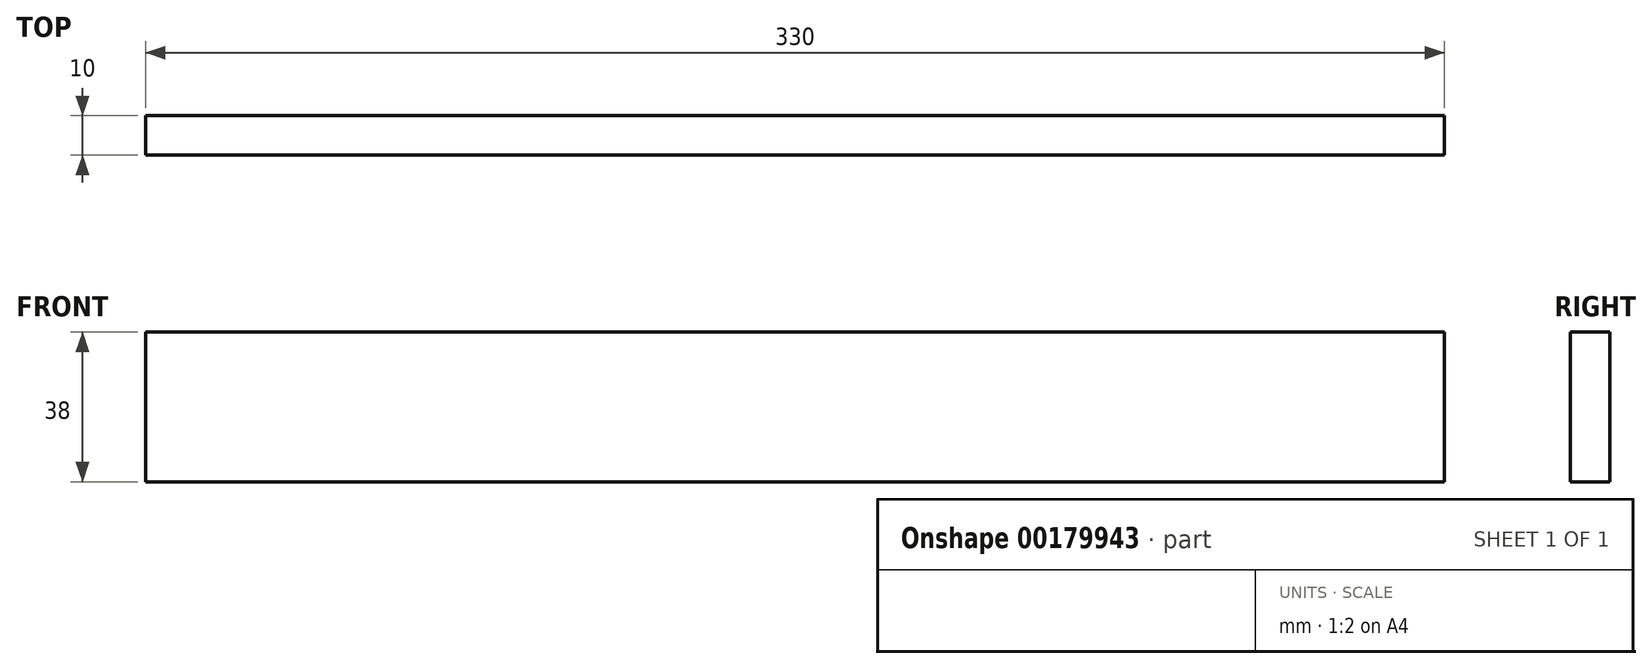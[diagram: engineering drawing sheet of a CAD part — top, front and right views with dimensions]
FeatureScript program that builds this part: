
annotation { "Feature Type Name" : "Feature", "Feature Type Description" : "" }
export const myFeature = defineFeature(function(context is Context, id is Id, definition is map)
    precondition{}
    {
        {
            var Q0;
            Q0=qCreatedBy(makeId("Front.planeOp"),FACE);
            var sketch = newSketch(context, id + "F0", { "sketchPlane" : qUnion([Q0])});
            skLineSegment(sketch, "E0.bottom", {"start": v(0, 0) * mm, "end": v(330, 0) * mm});
            skLineSegment(sketch, "E0.top", {"start": v(0, 38) * mm, "end": v(330, 38) * mm});
            skLineSegment(sketch, "E0.left", {"start": v(0, 0) * mm, "end": v(0, 38) * mm});
            skLineSegment(sketch, "E0.right", {"start": v(330, 0) * mm, "end": v(330, 38) * mm});
            skSolve(sketch);
        }
        {
            var Q0;
            Q0=qSketchRegion(id+"F0",true);
            extrude(context, id + "F1", {"entities" : qUnion([Q0]), "depth" : 10 * mm});
        }
    });
